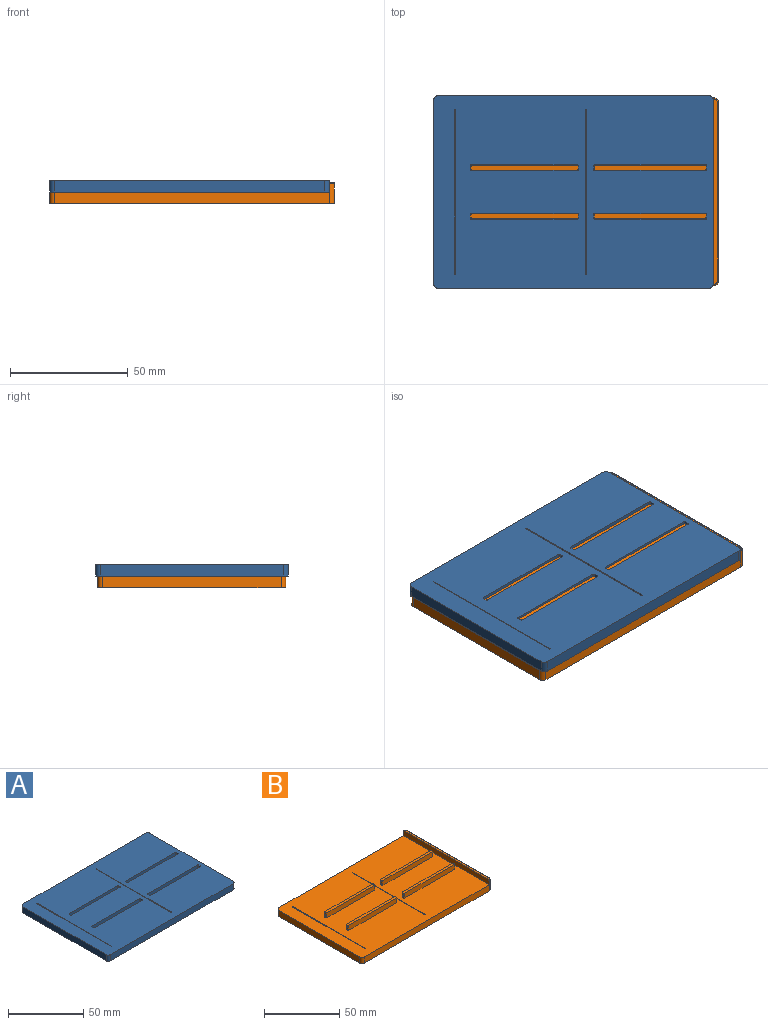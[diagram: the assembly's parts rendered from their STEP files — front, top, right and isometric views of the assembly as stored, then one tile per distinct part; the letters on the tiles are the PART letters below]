
ASSEMBLY  parts=2 mates=1
PART A: 58 faces, bbox 119.1x82x5 mm
  f0: plane 119.1x82mm, normal (0,0,1), area 9223.6mm2, adj f2,f3,f4,f5,f6,f7,f8,f9
  f1: plane 119.1x82mm, normal (0,0,-1), area 9223.6mm2, adj f2,f3,f4,f5,f6,f7,f8,f9
  f2: plane 115.1x5mm, normal (0,1,0), area 575.5mm2, adj f0,f1,f30,f33
  f3: plane 78x5mm, normal (-1,0,0), area 390mm2, adj f0,f1,f30,f31
  f4: plane 115.1x5mm, normal (0,-1,0), area 575.5mm2, adj f0,f1,f31,f32
  f5: plane 78x5mm, normal (1,0,0), area 390mm2, adj f0,f1,f32,f33
  f6: plane 5x0.3mm, normal (0,1,0), area 1.5mm2, adj f0,f1,f54,f57
  f7: plane 69.8x5mm, normal (-1,0,0), area 349mm2, adj f0,f1,f54,f55
  f8: plane 5x0.3mm, normal (0,-1,0), area 1.5mm2, adj f0,f1,f55,f56
  f9: plane 69.8x5mm, normal (1,0,0), area 349mm2, adj f0,f1,f56,f57
  f10: plane 45x5mm, normal (0,1,0), area 225mm2, adj f0,f1,f42,f45
  f11: plane 5x1.5mm, normal (-1,0,0), area 7.5mm2, adj f0,f1,f42,f43
  f12: plane 45x5mm, normal (0,-1,0), area 225mm2, adj f0,f1,f43,f44
  f13: plane 5x1.5mm, normal (1,0,0), area 7.5mm2, adj f0,f1,f44,f45
  f14: plane 5x1.5mm, normal (-1,0,0), area 7.5mm2, adj f0,f1,f46,f47
  f15: plane 45x5mm, normal (0,-1,0), area 225mm2, adj f0,f1,f46,f49
  f16: plane 5x1.5mm, normal (1,0,0), area 7.5mm2, adj f0,f1,f48,f49
  f17: plane 45x5mm, normal (0,1,0), area 225mm2, adj f0,f1,f47,f48
  f18: plane 5x1.5mm, normal (-1,0,0), area 7.5mm2, adj f0,f1,f34,f37
  f19: plane 47x5mm, normal (0,-1,0), area 235mm2, adj f0,f1,f34,f35
  f20: plane 5x1.5mm, normal (1,0,0), area 7.5mm2, adj f0,f1,f35,f36
  f21: plane 47x5mm, normal (0,1,0), area 235mm2, adj f0,f1,f36,f37
  f22: plane 5x1.5mm, normal (1,0,0), area 7.5mm2, adj f0,f1,f38,f41
  f23: plane 47x5mm, normal (0,1,0), area 235mm2, adj f0,f1,f40,f41
  f24: plane 5x1.5mm, normal (-1,0,0), area 7.5mm2, adj f0,f1,f39,f40
  f25: plane 47x5mm, normal (0,-1,0), area 235mm2, adj f0,f1,f38,f39
  f26: plane 69.8x5mm, normal (1,0,0), area 349mm2, adj f0,f1,f50,f53
  f27: plane 5x0.3mm, normal (0,1,0), area 1.5mm2, adj f0,f1,f50,f51
  f28: plane 69.8x5mm, normal (-1,0,0), area 349mm2, adj f0,f1,f51,f52
  f29: plane 5x0.3mm, normal (0,-1,0), area 1.5mm2, adj f0,f1,f52,f53
  f30: cylinder r=2mm len=5mm, axis (0,0,-1), area 15.7mm2, adj f0,f1,f2,f3
  f31: cylinder r=2mm len=5mm, axis (0,0,1), area 15.7mm2, adj f0,f1,f3,f4
  f32: cylinder r=2mm len=5mm, axis (0,0,-1), area 15.7mm2, adj f0,f1,f4,f5
  f33: cylinder r=2mm len=5mm, axis (0,0,1), area 15.7mm2, adj f0,f1,f2,f5
  f34: cylinder r=0.5mm len=5mm, axis (0,0,-1), area 3.9mm2, adj f0,f1,f18,f19
  f35: cylinder r=0.5mm len=5mm, axis (0,0,-1), area 3.9mm2, adj f0,f1,f19,f20
  f36: cylinder r=0.5mm len=5mm, axis (0,0,-1), area 3.9mm2, adj f0,f1,f20,f21
  f37: cylinder r=0.5mm len=5mm, axis (0,0,-1), area 3.9mm2, adj f0,f1,f18,f21
  f38: cylinder r=0.5mm len=5mm, axis (0,0,-1), area 3.9mm2, adj f0,f1,f22,f25
  f39: cylinder r=0.5mm len=5mm, axis (0,0,-1), area 3.9mm2, adj f0,f1,f24,f25
  f40: cylinder r=0.5mm len=5mm, axis (0,0,-1), area 3.9mm2, adj f0,f1,f23,f24
  f41: cylinder r=0.5mm len=5mm, axis (0,0,-1), area 3.9mm2, adj f0,f1,f22,f23
  f42: cylinder r=0.5mm len=5mm, axis (0,0,1), area 3.9mm2, adj f0,f1,f10,f11
  f43: cylinder r=0.5mm len=5mm, axis (0,0,1), area 3.9mm2, adj f0,f1,f11,f12
  f44: cylinder r=0.5mm len=5mm, axis (0,0,-1), area 3.9mm2, adj f0,f1,f12,f13
  f45: cylinder r=0.5mm len=5mm, axis (0,0,-1), area 3.9mm2, adj f0,f1,f10,f13
  f46: cylinder r=0.5mm len=5mm, axis (0,0,1), area 3.9mm2, adj f0,f1,f14,f15
  f47: cylinder r=0.5mm len=5mm, axis (0,0,-1), area 3.9mm2, adj f0,f1,f14,f17
  f48: cylinder r=0.5mm len=5mm, axis (0,0,1), area 3.9mm2, adj f0,f1,f16,f17
  f49: cylinder r=0.5mm len=5mm, axis (0,0,-1), area 3.9mm2, adj f0,f1,f15,f16
  f50: cylinder r=0.1mm len=5mm, axis (0,0,-1), area 0.8mm2, adj f0,f1,f26,f27
  f51: cylinder r=0.1mm len=5mm, axis (0,0,1), area 0.8mm2, adj f0,f1,f27,f28
  f52: cylinder r=0.1mm len=5mm, axis (0,0,-1), area 0.8mm2, adj f0,f1,f28,f29
  f53: cylinder r=0.1mm len=5mm, axis (0,0,1), area 0.8mm2, adj f0,f1,f26,f29
  f54: cylinder r=0.1mm len=5mm, axis (0,0,-1), area 0.8mm2, adj f0,f1,f6,f7
  f55: cylinder r=0.1mm len=5mm, axis (0,0,-1), area 0.8mm2, adj f0,f1,f7,f8
  f56: cylinder r=0.1mm len=5mm, axis (0,0,-1), area 0.8mm2, adj f0,f1,f8,f9
  f57: cylinder r=0.1mm len=5mm, axis (0,0,-1), area 0.8mm2, adj f0,f1,f6,f9
PART B: 67 faces, bbox 121.3x80.3x9 mm
  f0: plane 119.1x80mm, normal (0,0,1), area 9084.8mm2, adj f2,f3,f4,f5,f6,f7,f8,f9
  f1: plane 121.1x80mm, normal (0,0,-1), area 9616.6mm2, adj f2,f3,f4,f5,f6,f7,f8,f29
  f2: plane 117.1x5mm, normal (0,1,0), area 585.5mm2, adj f0,f1,f36,f38
  f3: plane 76x5mm, normal (-1,0,0), area 380mm2, adj f0,f1,f38,f39
  f4: plane 117.1x5mm, normal (0,-1,0), area 585.5mm2, adj f0,f1,f37,f39
  f5: plane 5x0.3mm, normal (0,1,0), area 1.5mm2, adj f0,f1,f60,f63
  f6: plane 67.8x5mm, normal (-1,0,0), area 339mm2, adj f0,f1,f60,f61
  f7: plane 5x0.3mm, normal (0,-1,0), area 1.5mm2, adj f0,f1,f61,f62
  f8: plane 67.8x5mm, normal (1,0,0), area 339mm2, adj f0,f1,f62,f63
  f9: plane 4x1mm, normal (1,0,0), area 4mm2, adj f0,f13,f48,f49
  f10: plane 44.8x4mm, normal (0,1,0), area 179.2mm2, adj f0,f13,f48,f51
  f11: plane 4x1mm, normal (-1,0,0), area 4mm2, adj f0,f13,f50,f51
  f12: plane 44.8x4mm, normal (0,-1,0), area 179.2mm2, adj f0,f13,f49,f50
  f13: plane 45.8x2mm, normal (0,0,1), area 91.4mm2, adj f9,f10,f11,f12,f48,f49,f50,f51
  f14: plane 44.8x4mm, normal (0,-1,0), area 179.2mm2, adj f0,f18,f52,f55
  f15: plane 4x1mm, normal (1,0,0), area 4mm2, adj f0,f18,f52,f53
  f16: plane 44.8x4mm, normal (0,1,0), area 179.2mm2, adj f0,f18,f53,f54
  f17: plane 4x1mm, normal (-1,0,0), area 4mm2, adj f0,f18,f54,f55
  f18: plane 45.8x2mm, normal (0,0,1), area 91.4mm2, adj f14,f15,f16,f17,f52,f53,f54,f55
  f19: plane 4x1mm, normal (-1,0,0), area 4mm2, adj f0,f23,f40,f43
  f20: plane 46.8x4mm, normal (0,-1,0), area 187.2mm2, adj f0,f23,f42,f43
  f21: plane 4x1mm, normal (1,0,0), area 4mm2, adj f0,f23,f41,f42
  f22: plane 46.8x4mm, normal (0,1,0), area 187.2mm2, adj f0,f23,f40,f41
  f23: plane 47.8x2mm, normal (0,0,1), area 95.4mm2, adj f19,f20,f21,f22,f40,f41,f42,f43
  f24: plane 4x1mm, normal (1,0,0), area 4mm2, adj f0,f28,f44,f47
  f25: plane 46.8x4mm, normal (0,1,0), area 187.2mm2, adj f0,f28,f44,f45
  f26: plane 4x1mm, normal (-1,0,0), area 4mm2, adj f0,f28,f45,f46
  f27: plane 46.8x4mm, normal (0,-1,0), area 187.2mm2, adj f0,f28,f46,f47
  f28: plane 47.8x2mm, normal (0,0,1), area 95.4mm2, adj f24,f25,f26,f27,f44,f45,f46,f47
  f29: plane 67.8x5mm, normal (1,0,0), area 339mm2, adj f0,f1,f56,f59
  f30: plane 5x0.3mm, normal (0,1,0), area 1.5mm2, adj f0,f1,f56,f57
  f31: plane 67.8x5mm, normal (-1,0,0), area 339mm2, adj f0,f1,f57,f58
  f32: plane 5x0.3mm, normal (0,-1,0), area 1.5mm2, adj f0,f1,f58,f59
  f33: plane 76x8.5mm, normal (1,0,0), area 646mm2, adj f1,f36,f37,f65
  f34: plane 80x4mm, normal (-1,0,0), area 319.9mm2, adj f0,f35,f36,f37,f64,f66
  f35: plane 79x1.5mm, normal (0,0,1), area 117.5mm2, adj f34,f64,f65,f66
  f36: cylinder r=2mm len=8.5mm, axis (0,0,-1), area 26.7mm2, adj f1,f2,f33,f34,f64
  f37: cylinder r=2mm len=8.5mm, axis (0,0,1), area 26.7mm2, adj f1,f4,f33,f34,f66
  f38: cylinder r=2mm len=5mm, axis (0,0,-1), area 15.7mm2, adj f0,f1,f2,f3
  f39: cylinder r=2mm len=5mm, axis (0,0,1), area 15.7mm2, adj f0,f1,f3,f4
  f40: cylinder r=0.5mm len=4mm, axis (0,0,-1), area 3.1mm2, adj f0,f19,f22,f23
  f41: cylinder r=0.5mm len=4mm, axis (0,0,-1), area 3.1mm2, adj f0,f21,f22,f23
  f42: cylinder r=0.5mm len=4mm, axis (0,0,-1), area 3.1mm2, adj f0,f20,f21,f23
  f43: cylinder r=0.5mm len=4mm, axis (0,0,-1), area 3.1mm2, adj f0,f19,f20,f23
  f44: cylinder r=0.5mm len=4mm, axis (0,0,-1), area 3.1mm2, adj f0,f24,f25,f28
  f45: cylinder r=0.5mm len=4mm, axis (0,0,-1), area 3.1mm2, adj f0,f25,f26,f28
  f46: cylinder r=0.5mm len=4mm, axis (0,0,-1), area 3.1mm2, adj f0,f26,f27,f28
  f47: cylinder r=0.5mm len=4mm, axis (0,0,-1), area 3.1mm2, adj f0,f24,f27,f28
  f48: cylinder r=0.5mm len=4mm, axis (0,0,1), area 3.1mm2, adj f0,f9,f10,f13
  f49: cylinder r=0.5mm len=4mm, axis (0,0,-1), area 3.1mm2, adj f0,f9,f12,f13
  f50: cylinder r=0.5mm len=4mm, axis (0,0,1), area 3.1mm2, adj f0,f11,f12,f13
  f51: cylinder r=0.5mm len=4mm, axis (0,0,-1), area 3.1mm2, adj f0,f10,f11,f13
  f52: cylinder r=0.5mm len=4mm, axis (0,0,1), area 3.1mm2, adj f0,f14,f15,f18
  f53: cylinder r=0.5mm len=4mm, axis (0,0,1), area 3.1mm2, adj f0,f15,f16,f18
  f54: cylinder r=0.5mm len=4mm, axis (0,0,-1), area 3.1mm2, adj f0,f16,f17,f18
  f55: cylinder r=0.5mm len=4mm, axis (0,0,-1), area 3.1mm2, adj f0,f14,f17,f18
  f56: cylinder r=0.1mm len=5mm, axis (0,0,-1), area 0.8mm2, adj f0,f1,f29,f30
  f57: cylinder r=0.1mm len=5mm, axis (0,0,1), area 0.8mm2, adj f0,f1,f30,f31
  f58: cylinder r=0.1mm len=5mm, axis (0,0,-1), area 0.8mm2, adj f0,f1,f31,f32
  f59: cylinder r=0.1mm len=5mm, axis (0,0,1), area 0.8mm2, adj f0,f1,f29,f32
  f60: cylinder r=0.1mm len=5mm, axis (0,0,-1), area 0.8mm2, adj f0,f1,f5,f6
  f61: cylinder r=0.1mm len=5mm, axis (0,0,-1), area 0.8mm2, adj f0,f1,f6,f7
  f62: cylinder r=0.1mm len=5mm, axis (0,0,-1), area 0.8mm2, adj f0,f1,f7,f8
  f63: cylinder r=0.1mm len=5mm, axis (0,0,-1), area 0.8mm2, adj f0,f1,f5,f8
  f64: torus R=1.5mm, axis (0,0,1), area 2.2mm2, adj f34,f35,f36,f65
  f65: cylinder r=0.5mm len=76mm, axis (0,1,0), area 59.7mm2, adj f33,f35,f64,f66
  f66: torus R=1.5mm, axis (0,0,1), area 2.2mm2, adj f34,f35,f37,f65
PLACE A t=(57.11,7.41,25.56)mm
PLACE B t=(57.21,8.51,20.56)mm
MATE fastened A.f37 <-> B.f0  axis (0,0,-1) through (172.71,37.26,25.56)mm
